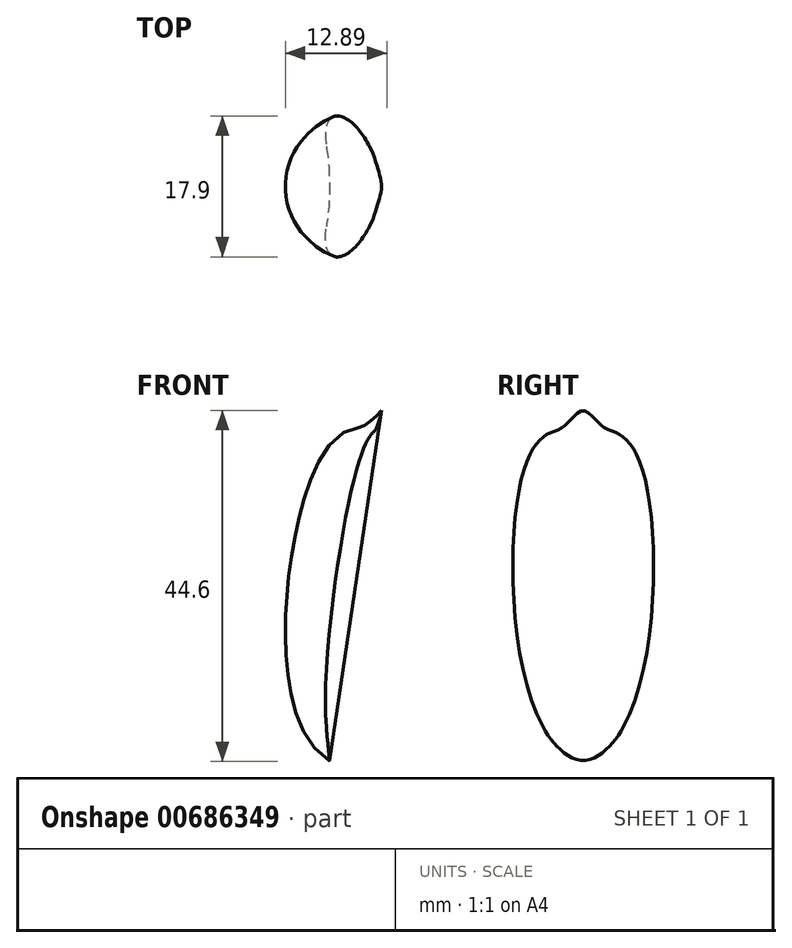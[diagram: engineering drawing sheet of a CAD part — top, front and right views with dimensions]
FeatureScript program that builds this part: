
annotation { "Feature Type Name" : "Feature", "Feature Type Description" : "" }
export const myFeature = defineFeature(function(context is Context, id is Id, definition is map)
    precondition{}
    {
        {
            var Q0;
            Q0=qCreatedBy(makeId("Front.planeOp"),FACE);
            var sketch = newSketch(context, id + "F0", { "sketchPlane" : qUnion([Q0])});
            skFitSpline(sketch, "E0", {"points": [v(6.95, 46.73) * mm, v(1.59, 42.54) * mm, v(-3.52, 36) * mm, v(0, 0) * mm], "startDerivative": vector(-41.6, -56.18) * mm, "endDerivative": vector(54.13, -22.01) * mm});
            skLineSegment(sketch, "E1", {"start": v(6.95, 46.73) * mm, "end": v(0, 0) * mm});
            skSolve(sketch);
        }
        {
            var Q0;
            Q0 = qSketchRegion(id + "F0", true);
            var Q1;
            Q1=sQuery(id+"F0.wireOp",EDGE,"E1");
            revolve(context, id + "F1", {"entities" : qUnion([Q0]), "axis" : qUnion([Q1]), "revolveType" : RevolveType.SYMMETRIC, "angle" : 135 * degree});
        }
        {
            var Q0;
            Q0=makeQuery(id+"F1.opRevolve","CAP_EDGE",EDGE,{"disambiguationData":[OSD([sQuery(id+"F0.wireOp",EDGE,"E1")])],"isStart":true});
            fillet(context, id + "F2", {"entities" : qUnion([Q0]), "radius" : 13.26 * mm, "tangentPropagation" : true, "allowEdgeOverflow" : false});
        }
    });
